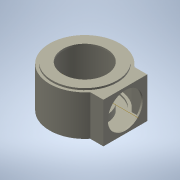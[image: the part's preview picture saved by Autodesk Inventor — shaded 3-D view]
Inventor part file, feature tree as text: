
AUTODESK INVENTOR PART (.ipt)
format: ipt  version: 2021 (Build 250183000, 183)  size: 194,560 bytes
history: native  units: mm (DEFAULTED — no unit token found)
features: extrude x5, sketch x4, other x3, hole x2, plane x2, shell x1
ambient origin geometry x8: Origin, YZ Plane, XZ Plane, XY Plane, X Axis, Y Axis, Z Axis, Center Point
bodies: Solid1 (feature_tree)
feature tree (17):
  extrude  "押し出し1"  Depth=40.0mm TaperAngle=0.0deg
  extrude  "押し出し2"  Depth=2.0mm TaperAngle=0.0deg
  other  "作業平面1"
  extrude  "押し出し3"  Depth=46.0mm
  other  "作業軸1"
  other  "Work Axis2"
  shell  "Shell1"  Thickness=25.0mm
  hole  "Hole1"  [1 undecoded]
  hole  "Hole2"  [1 undecoded]
  extrude  "Extrusion7"  Depth=10.0mm TaperAngle=0.0deg
  extrude  "Extrusion8"  [1 undecoded]
  plane  "Work Plane2"
  plane  "Work Plane3"
  sketch  "Sketch7"  dims[d0=80.0mm d1=40.0mm d2=0.0mm]
  sketch  "Sketch8"  dims[d3=3.0mm d4=2.0mm d5=0.0mm]
  sketch  "Sketch9"  dims[d6=50.0mm d7=46.0mm d8=25.0mm]
  sketch  "Sketch10"  dims[d9=46.2mm d10=0.0mm d20=2.0mm d21=50.0mm d22=6.0mm d23=4.0mm d24=2.0mm d25=14.3117mm d26=8.0mm d27=20.594885mm d28=40.0mm d29=6.0mm d30=4.0mm d31=2.0mm d32=14.3117mm d33=2.0mm d34=20.594885mm d35=10.0mm d36=0.0mm d37=10.0mm d38=0.0mm]
note: 3 required parameter values undecoded (feature->parameter linkage not recoverable at this tier; creation-order binding heuristic only, values carry confidence <= 0.55)
